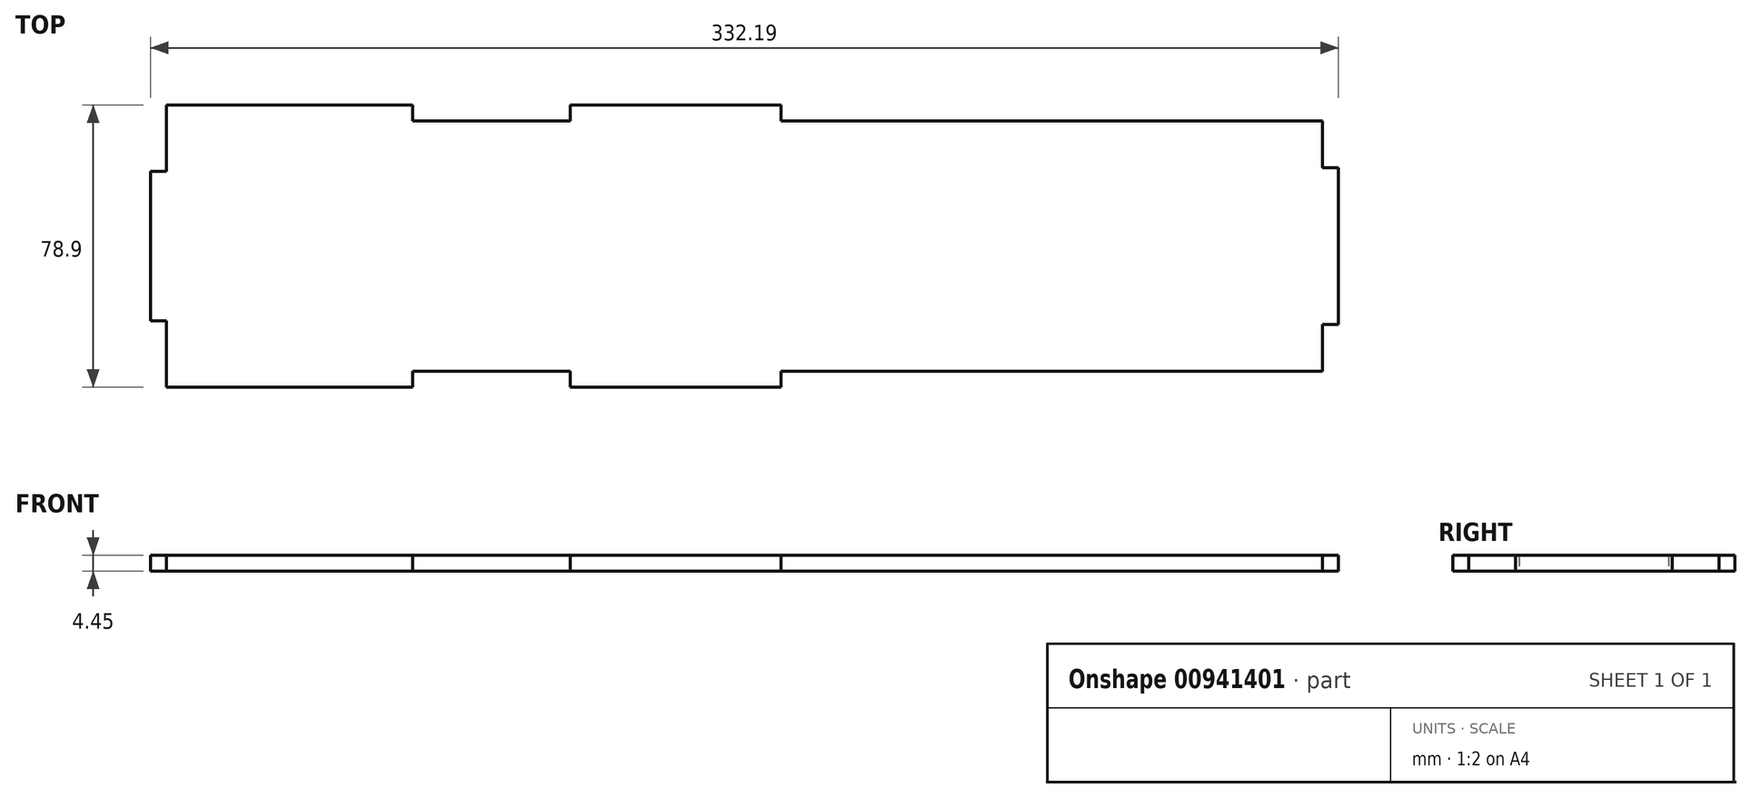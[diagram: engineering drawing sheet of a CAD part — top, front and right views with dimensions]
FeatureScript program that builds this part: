
annotation { "Feature Type Name" : "Feature", "Feature Type Description" : "" }
export const myFeature = defineFeature(function(context is Context, id is Id, definition is map)
    precondition{}
    {
        {
            var Q0;
            Q0=qCreatedBy(makeId("Top.planeOp"),FACE);
            var sketch = newSketch(context, id + "F0", { "sketchPlane" : qUnion([Q0])});
            skLineSegment(sketch, "E0.bottom", {"start": v(27.05, -35) * mm, "end": v(-17.05, -35) * mm});
            skLineSegment(sketch, "E0.top", {"start": v(27.05, 35) * mm, "end": v(-17.05, 35) * mm});
            skLineSegment(sketch, "E0.right", {"start": v(-85.95, -35) * mm, "end": v(-85.95, -20.89) * mm});
            skPoint(sketch, "E0.middle", {"position": v(0, 0) * mm});
            skLineSegment(sketch, "E1.top", {"start": v(-85.95, 39.45) * mm, "end": v(-17.05, 39.45) * mm});
            skLineSegment(sketch, "E1.left", {"start": v(-85.95, 35) * mm, "end": v(-85.95, 39.45) * mm});
            skLineSegment(sketch, "E1.right", {"start": v(-17.05, 35) * mm, "end": v(-17.05, 39.45) * mm});
            skLineSegment(sketch, "E2.top", {"start": v(85.95, 39.45) * mm, "end": v(27.05, 39.45) * mm});
            skLineSegment(sketch, "E2.left", {"start": v(85.95, 35) * mm, "end": v(85.95, 39.45) * mm});
            skLineSegment(sketch, "E2.right", {"start": v(27.05, 35) * mm, "end": v(27.05, 39.45) * mm});
            skLineSegment(sketch, "E3.MirrorCS", {"start": v(-85.95, -39.45) * mm, "end": v(-17.05, -39.45) * mm});
            skLineSegment(sketch, "E4.MirrorCS", {"start": v(-85.95, -35) * mm, "end": v(-85.95, -39.45) * mm});
            skLineSegment(sketch, "E5.MirrorCS", {"start": v(-17.05, -35) * mm, "end": v(-17.05, -39.45) * mm});
            skLineSegment(sketch, "E6.MirrorCS", {"start": v(27.05, -35) * mm, "end": v(27.05, -39.45) * mm});
            skLineSegment(sketch, "E7.MirrorCS", {"start": v(85.95, -39.45) * mm, "end": v(27.05, -39.45) * mm});
            skLineSegment(sketch, "E8.MirrorCS", {"start": v(85.95, -35) * mm, "end": v(85.95, -39.45) * mm});
            skLineSegment(sketch, "E9.bottom", {"start": v(-90.4, -20.89) * mm, "end": v(-85.95, -20.89) * mm});
            skLineSegment(sketch, "E9.top", {"start": v(-90.4, 20.89) * mm, "end": v(-85.95, 20.89) * mm});
            skLineSegment(sketch, "E9.left", {"start": v(-90.4, -20.89) * mm, "end": v(-90.4, 20.89) * mm});
            skPoint(sketch, "E9.middle", {"position": v(-85.95, 0) * mm});
            skLineSegment(sketch, "E10.trimOffspring", {"start": v(-85.95, 20.89) * mm, "end": v(-85.95, 35) * mm});
            skPoint(sketch, "E11.orphan", {"position": v(-81.5, -20.89) * mm});
            skPoint(sketch, "E12.orphan", {"position": v(-81.5, 20.89) * mm});
            skLineSegment(sketch, "E13.bottom", {"start": v(85.95, -35) * mm, "end": v(237.34, -35) * mm});
            skLineSegment(sketch, "E13.top", {"start": v(85.95, 35) * mm, "end": v(237.34, 35) * mm});
            skLineSegment(sketch, "E13.right", {"start": v(237.34, -35) * mm, "end": v(237.34, -21.89) * mm});
            skPoint(sketch, "E14.trimOffspring.start.orphan", {"position": v(237.34, 21.89) * mm});
            skPoint(sketch, "E0.left.end.orphan", {"position": v(237.34, -21.89) * mm});
            skLineSegment(sketch, "E15.MirrorCS", {"start": v(241.8, -21.89) * mm, "end": v(237.34, -21.89) * mm});
            skLineSegment(sketch, "E16.MirrorCS", {"start": v(241.8, -21.89) * mm, "end": v(241.8, 21.89) * mm});
            skLineSegment(sketch, "E17.MirrorCS", {"start": v(241.8, 21.89) * mm, "end": v(237.34, 21.89) * mm});
            skLineSegment(sketch, "E18.trimOffspring", {"start": v(237.34, 21.89) * mm, "end": v(237.34, 35) * mm});
            skSolve(sketch);
        }
        {
            var Q0;
            Q0=makeQuery(id+"F0.imprint","IMPRINT",FACE,{"disambiguationData":[TD([[makeQuery(id+"F0.imprint","IMPRINT",EDGE,{"derivedFrom":sQuery(id+"F0.wireOp",EDGE,"E0.top")}),1.0]])]});
            extrude(context, id + "F1", {"entities" : qUnion([Q0]), "depth" : 4.45 * mm, "offsetDistance" : 25 * mm});
        }
    });
